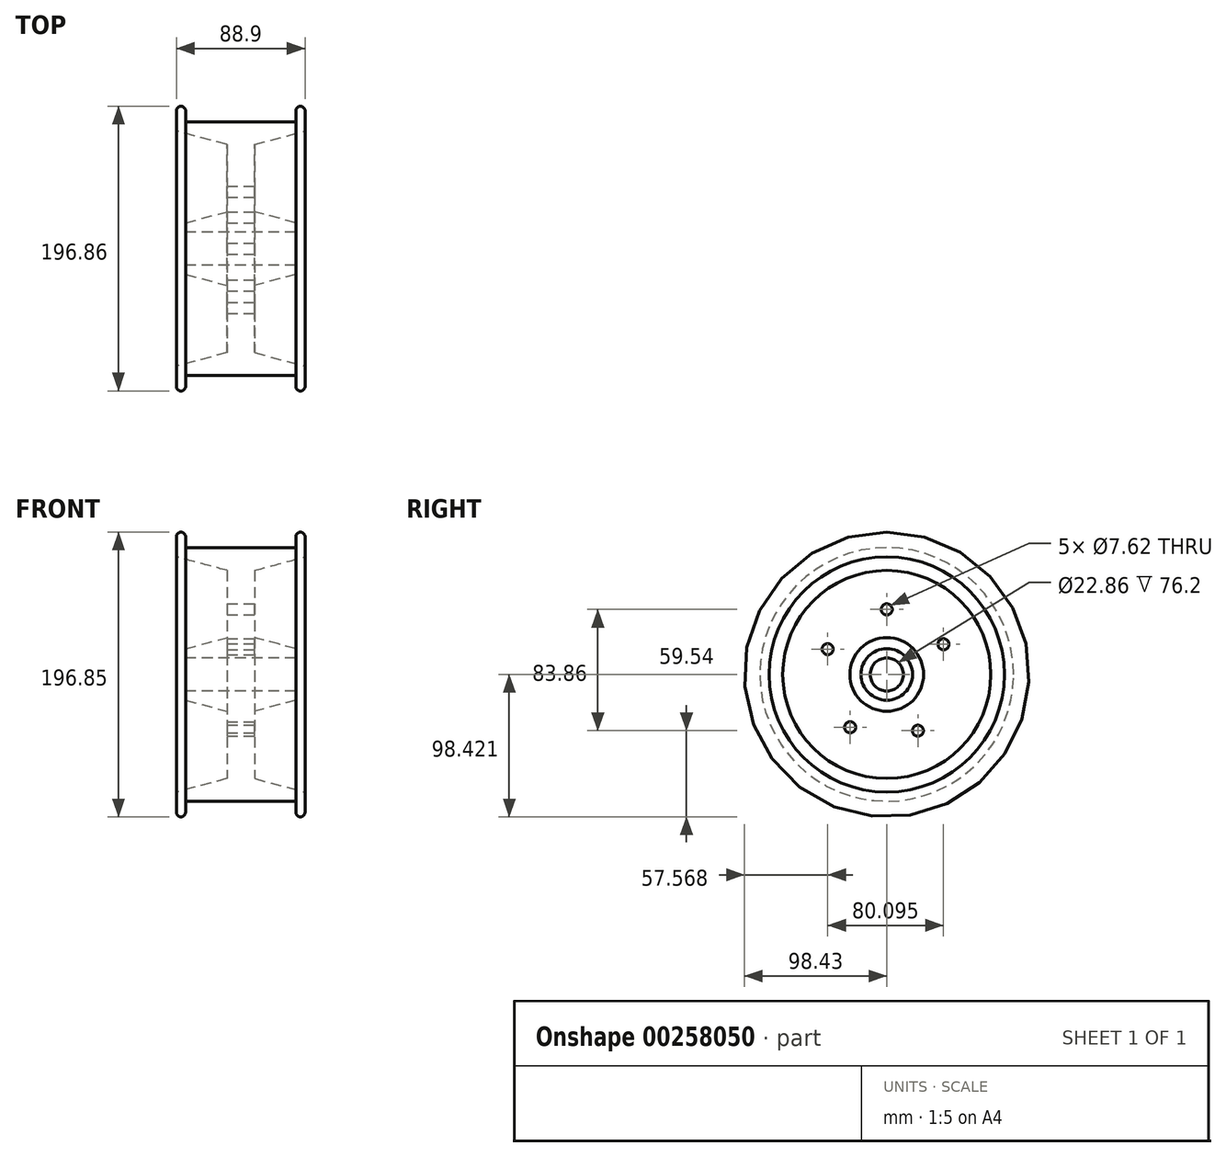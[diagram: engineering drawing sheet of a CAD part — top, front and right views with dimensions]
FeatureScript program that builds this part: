
annotation { "Feature Type Name" : "Feature", "Feature Type Description" : "" }
export const myFeature = defineFeature(function(context is Context, id is Id, definition is map)
    precondition{}
    {
        {
            var Q0;
            Q0=qCreatedBy(makeId("Front.planeOp"),FACE);
            var sketch = newSketch(context, id + "F0", { "sketchPlane" : qUnion([Q0])});
            skLineSegment(sketch, "E0", {"start": v(-38.1, -33.55) * mm, "end": v(0, -33.55) * mm});
            skLineSegment(sketch, "E1", {"start": v(-38.1, -33.55) * mm, "end": v(-38.1, -27.2) * mm});
            skLineSegment(sketch, "E2", {"start": v(-38.1, -27.2) * mm, "end": v(-9.52, -19.54) * mm});
            skLineSegment(sketch, "E3", {"start": v(-9.52, -19.54) * mm, "end": v(-9.53, 26.94) * mm});
            skLineSegment(sketch, "E4", {"start": v(-9.53, 26.94) * mm, "end": v(-44.45, 36.3) * mm});
            skLineSegment(sketch, "E5", {"start": v(-44.45, 36.3) * mm, "end": v(-44.45, 50.27) * mm});
            skLineSegment(sketch, "E6", {"start": v(-38.1, 50.27) * mm, "end": v(-38.1, 42.65) * mm});
            skLineSegment(sketch, "E7", {"start": v(-38.1, 42.65) * mm, "end": v(0, 42.65) * mm});
            skLineSegment(sketch, "E8", {"start": v(0, 42.65) * mm, "end": v(38.1, 42.65) * mm});
            skLineSegment(sketch, "E9", {"start": v(38.1, 42.65) * mm, "end": v(38.1, 50.27) * mm});
            skLineSegment(sketch, "E10", {"start": v(0, -33.55) * mm, "end": v(38.1, -33.55) * mm});
            skLineSegment(sketch, "E11", {"start": v(38.1, -33.55) * mm, "end": v(38.1, -27.2) * mm});
            skLineSegment(sketch, "E12", {"start": v(38.1, -27.2) * mm, "end": v(9.53, -19.54) * mm});
            skLineSegment(sketch, "E13", {"start": v(9.53, -19.54) * mm, "end": v(9.52, 26.94) * mm});
            skLineSegment(sketch, "E14", {"start": v(9.52, 26.94) * mm, "end": v(44.45, 36.3) * mm});
            skArc(sketch, "E15", {"start": v(-38.1, 50.27) * mm, "mid": v(-41.28, 53.45) * mm, "end": v(-44.45, 50.27) * mm});
            skLineSegment(sketch, "E16", {"start": v(44.45, 36.3) * mm, "end": v(44.45, 50.27) * mm});
            skArc(sketch, "E17", {"start": v(44.45, 50.27) * mm, "mid": v(41.28, 53.45) * mm, "end": v(38.1, 50.27) * mm});
            skLineSegment(sketch, "E18", {"start": v(0, 61.42) * mm, "end": v(0, -44.98) * mm, "construction": true});
            skLineSegment(sketch, "E19", {"start": v(0, -44.98) * mm, "end": v(-99.97, -44.98) * mm, "construction": true});
            skLineSegment(sketch, "E20", {"start": v(-99.97, -44.98) * mm, "end": v(99.36, -44.98) * mm, "construction": true});
            skSolve(sketch);
        }
        {
            var Q0;
            Q0 = qSketchRegion(id + "F0", true);
            var Q1;
            Q1=sQuery(id+"F0.wireOp",EDGE,"E20");
            revolve(context, id + "F1", {"entities" : qUnion([Q0]), "axis" : qUnion([Q1]), "revolveType" : RevolveType.FULL});
        }
        {
            var Q0;
            Q0=makeQuery(id+"F1.opRevolve","SWEPT_FACE",FACE,{"disambiguationData":[OSD([sQuery(id+"F0.wireOp",EDGE,"E13")])]});
            var sketch = newSketch(context, id + "F2", { "sketchPlane" : qUnion([Q0])});
            skCircle(sketch, "E21", {"center": v(0, -44.98) * mm, "radius": 44.45 * mm, "construction": true});
            skCircle(sketch, "E22", {"center": v(0, 0) * mm, "radius": 3.81 * mm});
            skCircle(sketch, "E23", {"center": v(39.23, -24.08) * mm, "radius": 3.81 * mm});
            skCircle(sketch, "E24", {"center": v(-40.86, -27.48) * mm, "radius": 3.81 * mm});
            skCircle(sketch, "E25", {"center": v(-25.33, -81.5) * mm, "radius": 3.81 * mm});
            skCircle(sketch, "E26", {"center": v(21.54, -83.86) * mm, "radius": 3.81 * mm});
            skSolve(sketch);
        }
        {
            var Q0;
            Q0 = qSketchRegion(id + "F2", true);
            extrude(context, id + "F3", {"entities" : qUnion([Q0]), "operationType" : NewBodyOperationType.REMOVE, "endBound" : BoundingType.THROUGH_ALL, "oppositeDirection" : true, "depth" : 25.4 * mm});
        }
    });
